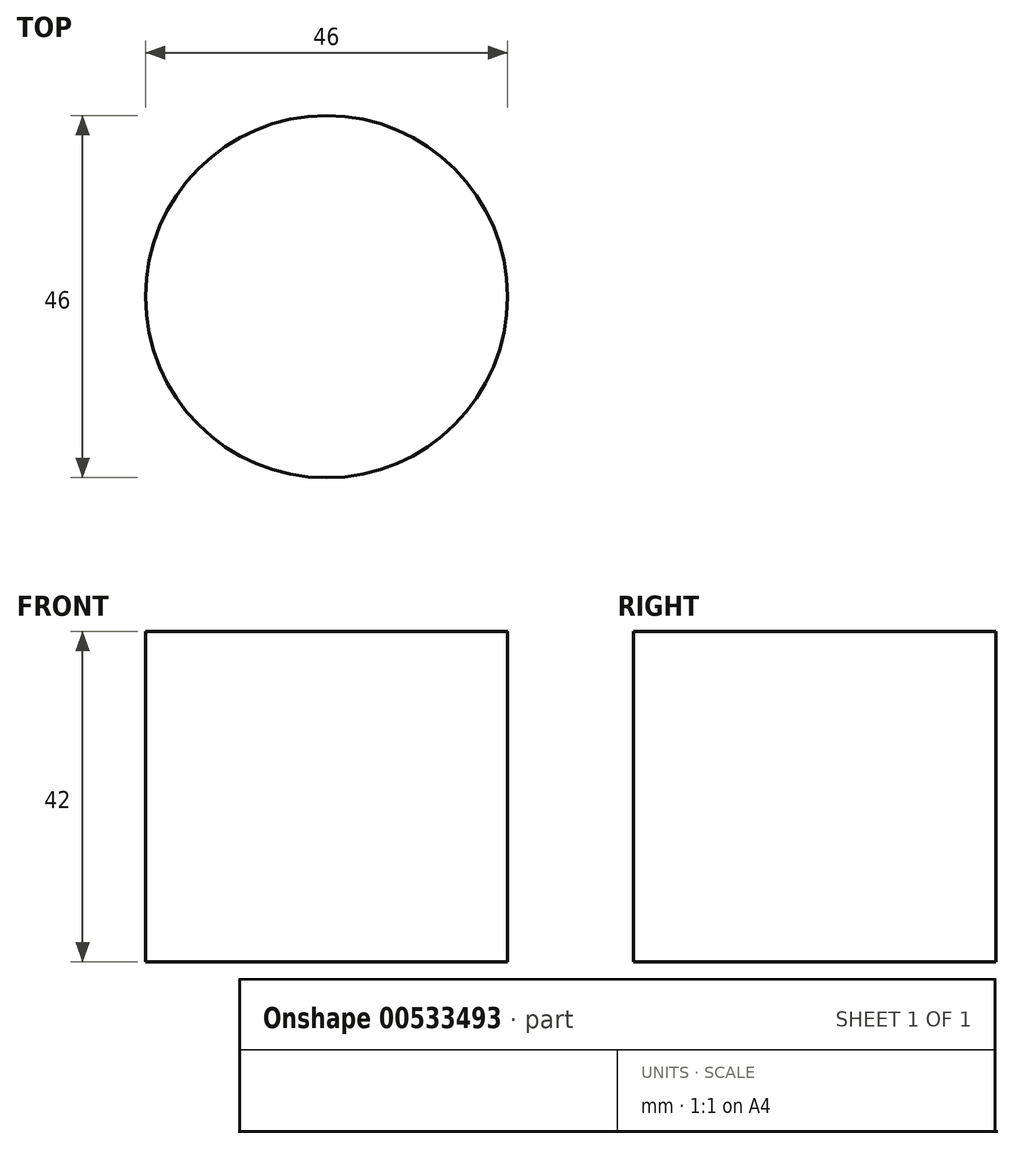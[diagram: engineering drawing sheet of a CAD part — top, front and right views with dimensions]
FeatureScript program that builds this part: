
annotation { "Feature Type Name" : "Feature", "Feature Type Description" : "" }
export const myFeature = defineFeature(function(context is Context, id is Id, definition is map)
    precondition{}
    {
        {
            var Q0;
            Q0=qCreatedBy(makeId("Top.planeOp"),FACE);
            var sketch = newSketch(context, id + "F0", { "sketchPlane" : qUnion([Q0])});
            skCircle(sketch, "E0", {"center": v(0, 0) * mm, "radius": 23 * mm});
            skSolve(sketch);
        }
        {
            var Q0;
            Q0=qSketchRegion(id+"F0",true);
            extrude(context, id + "F1", {"entities" : qUnion([Q0]), "depth" : 42 * mm, "offsetDistance" : 25 * mm});
        }
    });
